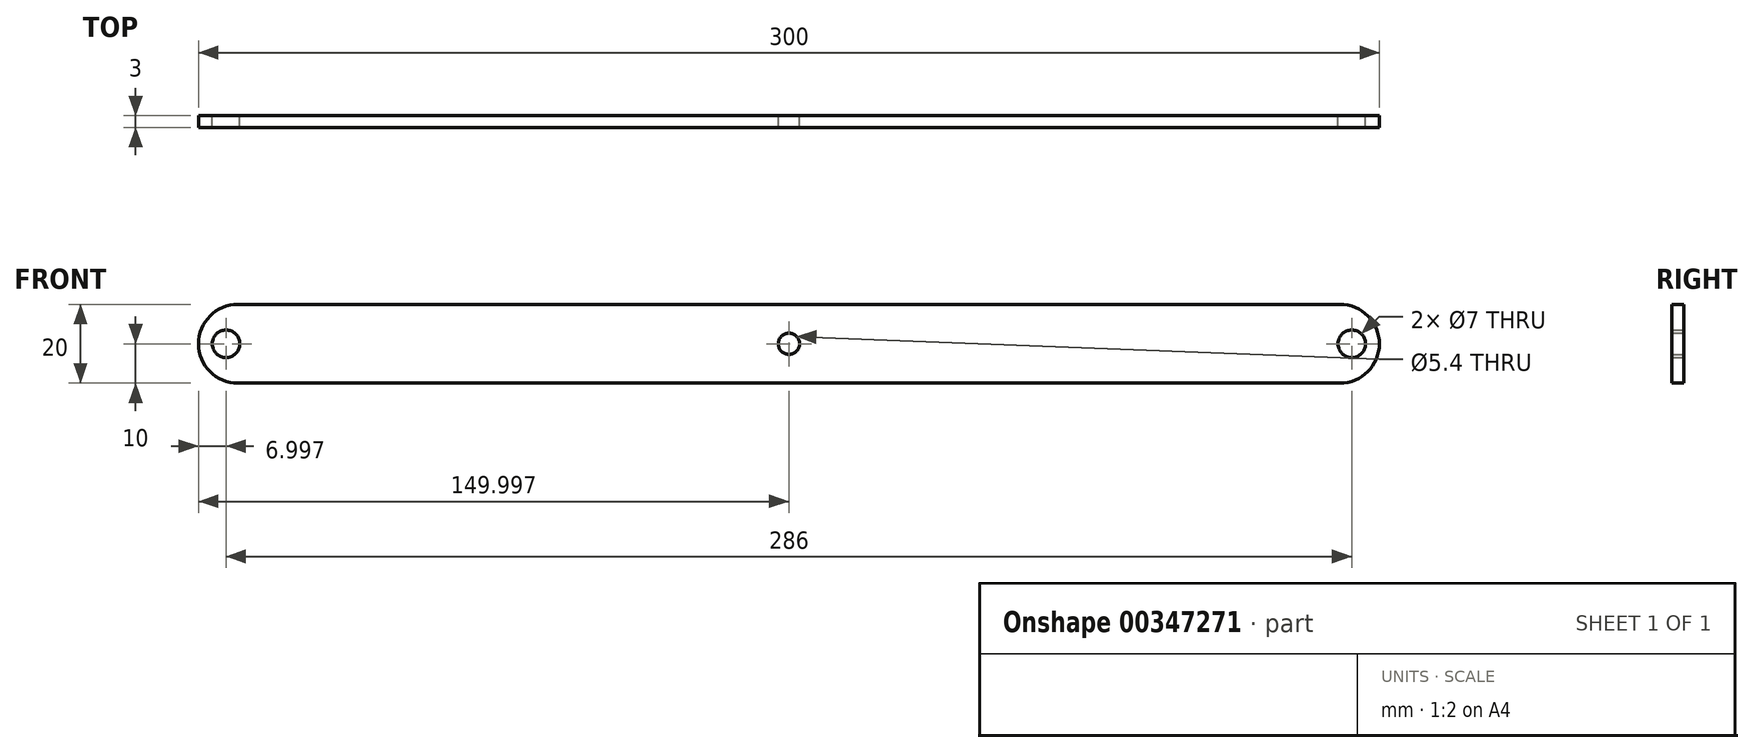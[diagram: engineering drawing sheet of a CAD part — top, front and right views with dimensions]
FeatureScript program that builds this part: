
annotation { "Feature Type Name" : "Feature", "Feature Type Description" : "" }
export const myFeature = defineFeature(function(context is Context, id is Id, definition is map)
    precondition{}
    {
        {
            var Q0;
            Q0=qCreatedBy(makeId("Front.planeOp"),FACE);
            var sketch = newSketch(context, id + "F0", { "sketchPlane" : qUnion([Q0])});
            skLineSegment(sketch, "E0.bottom", {"start": v(-140.06, 10) * mm, "end": v(139.94, 10) * mm});
            skLineSegment(sketch, "E0.top", {"start": v(-140.06, -10) * mm, "end": v(139.94, -10) * mm});
            skLineSegment(sketch, "E0.left", {"start": v(-150.06, 0) * mm, "end": v(-150.06, 0) * mm});
            skLineSegment(sketch, "E0.right", {"start": v(149.94, 0) * mm, "end": v(149.94, 0) * mm});
            skCircle(sketch, "E1", {"center": v(-0.06, 0) * mm, "radius": 2.7 * mm});
            skCircle(sketch, "E2", {"center": v(-143.06, 0) * mm, "radius": 3.5 * mm});
            skCircle(sketch, "E3", {"center": v(142.94, 0) * mm, "radius": 3.5 * mm});
            skPoint(sketch, "E4.visualSharp", {"position": v(-150.06, 10) * mm});
            skArc(sketch, "E4.filletArc", {"start": v(-140.06, 10) * mm, "mid": v(-147.13, 7.07) * mm, "end": v(-150.06, 0) * mm});
            skPoint(sketch, "E5.visualSharp", {"position": v(-150.06, -10) * mm});
            skArc(sketch, "E5.filletArc", {"start": v(-150.06, 0) * mm, "mid": v(-147.13, -7.07) * mm, "end": v(-140.06, -10) * mm});
            skPoint(sketch, "E6.visualSharp", {"position": v(149.94, 10) * mm});
            skArc(sketch, "E6.filletArc", {"start": v(149.94, 0) * mm, "mid": v(147, 7.07) * mm, "end": v(139.94, 10) * mm});
            skPoint(sketch, "E7.visualSharp", {"position": v(149.94, -10) * mm});
            skArc(sketch, "E7.filletArc", {"start": v(139.94, -10) * mm, "mid": v(147, -7.07) * mm, "end": v(149.94, 0) * mm});
            skSolve(sketch);
        }
        {
            var Q0;
            Q0 = qSketchRegion(id + "F0", true);
            extrude(context, id + "F1", {"entities" : qUnion([Q0]), "depth" : 3 * mm});
        }
    });
